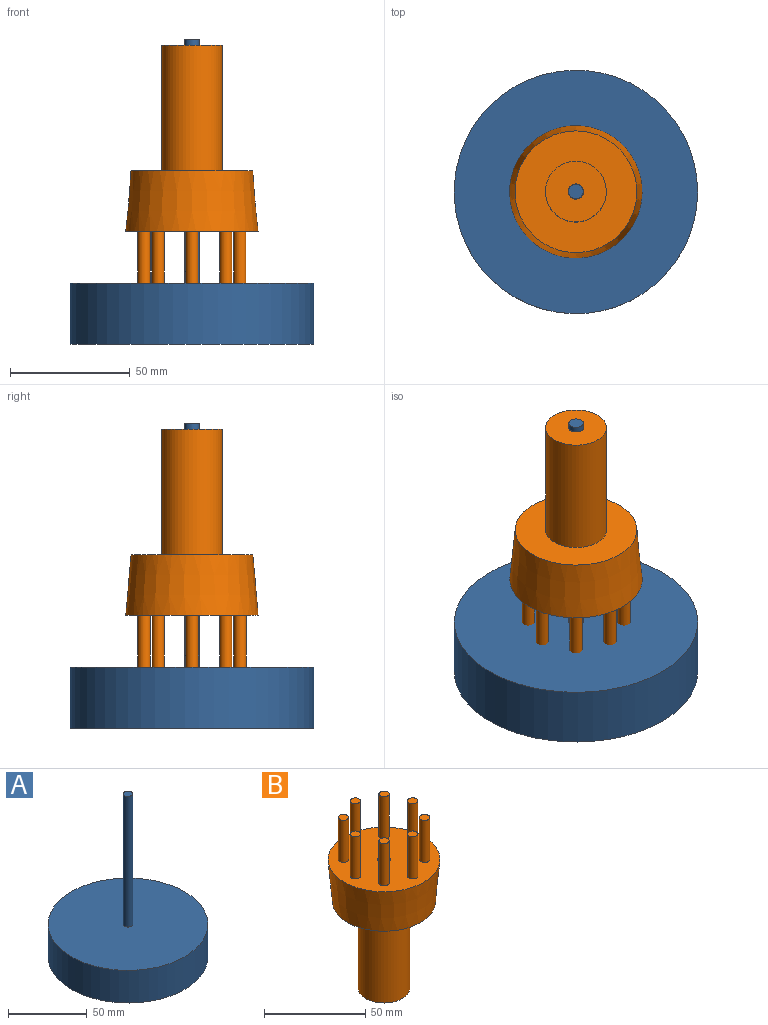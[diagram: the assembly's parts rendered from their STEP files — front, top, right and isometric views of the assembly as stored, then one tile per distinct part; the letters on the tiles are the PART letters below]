
ASSEMBLY  parts=2 mates=1
PART A: 5 faces, bbox 101.6x101.6x127 mm
  f0: plane 101.6x101.6mm, normal (0,0,-1), area 8107.3mm2, adj f4
  f1: plane 6.1x6.1mm, normal (0,0,1), area 29.2mm2, adj f2
  f2: cylinder r=3.05mm len=101.6mm, axis (0,0,1), area 1945.8mm2, adj f1,f3
  f3: plane 101.6x101.6mm, normal (0,0,1), area 8078.1mm2, adj f2,f4
  f4: cylinder r=50.8mm len=101.6mm, axis (0,0,1), area 8107.3mm2, adj f0,f3
PART B: 22 faces, bbox 55.2x55.2x103.1 mm
  f0: cylinder r=12.7mm len=52.32mm, axis (0,0,-1), area 4175.3mm2, adj f1,f4
  f1: plane 25.4x25.4mm, normal (0,0,-1), area 475mm2, adj f0,f5
  f2: cone r=25.4mm half-angle=5deg, axis (0,0,1), area 4247.1mm2, adj f3,f4
  f3: plane 55.24x55.24mm, normal (0,0,1), area 2203.2mm2, adj f2,f5,f6,f8,f10,f12,f14,f16
  f4: plane 50.8x50.8mm, normal (0,0,-1), area 1520.1mm2, adj f0,f2
  f5: cylinder r=3.17mm len=77.72mm, axis (0,0,-1), area 1550.5mm2, adj f1,f3
  f6: cylinder r=2.54mm len=25.4mm, axis (0,0,-1), area 405.4mm2, adj f3,f7
  f7: plane 5.08x5.08mm, normal (0,0,1), area 20.3mm2, adj f6
  f8: cylinder r=2.54mm len=25.4mm, axis (0,0,-1), area 405.4mm2, adj f3,f9
  f9: plane 5.08x5.08mm, normal (0,0,1), area 20.3mm2, adj f8
  f10: cylinder r=2.54mm len=25.4mm, axis (0,0,-1), area 405.4mm2, adj f3,f11
  f11: plane 5.08x5.08mm, normal (0,0,1), area 20.3mm2, adj f10
  f12: cylinder r=2.54mm len=25.4mm, axis (0,0,-1), area 405.4mm2, adj f3,f13
  f13: plane 5.08x5.08mm, normal (0,0,1), area 20.3mm2, adj f12
  f14: cylinder r=2.54mm len=25.4mm, axis (0,0,-1), area 405.4mm2, adj f3,f15
  f15: plane 5.08x5.08mm, normal (0,0,1), area 20.3mm2, adj f14
  f16: cylinder r=2.54mm len=25.4mm, axis (0,0,-1), area 405.4mm2, adj f3,f17
  f17: plane 5.08x5.08mm, normal (0,0,1), area 20.3mm2, adj f16
  f18: cylinder r=2.54mm len=25.4mm, axis (0,0,-1), area 405.4mm2, adj f3,f19
  f19: plane 5.08x5.08mm, normal (0,0,1), area 20.3mm2, adj f18
  f20: cylinder r=2.54mm len=25.4mm, axis (0,0,-1), area 405.4mm2, adj f3,f21
  f21: plane 5.08x5.08mm, normal (0,0,1), area 20.3mm2, adj f20
PLACE A rot(axis=(0.67,-0.58,-0.47),0deg) t=(-53.46,38.11,168.99)mm
PLACE B rot(axis=(-0.71,-0.71,0),180deg) t=(-53.46,38.11,293.76)mm
MATE slider B.f5 <-> A.f2  axis (0,0,1) through (-53.46,38.11,216.04)mm
